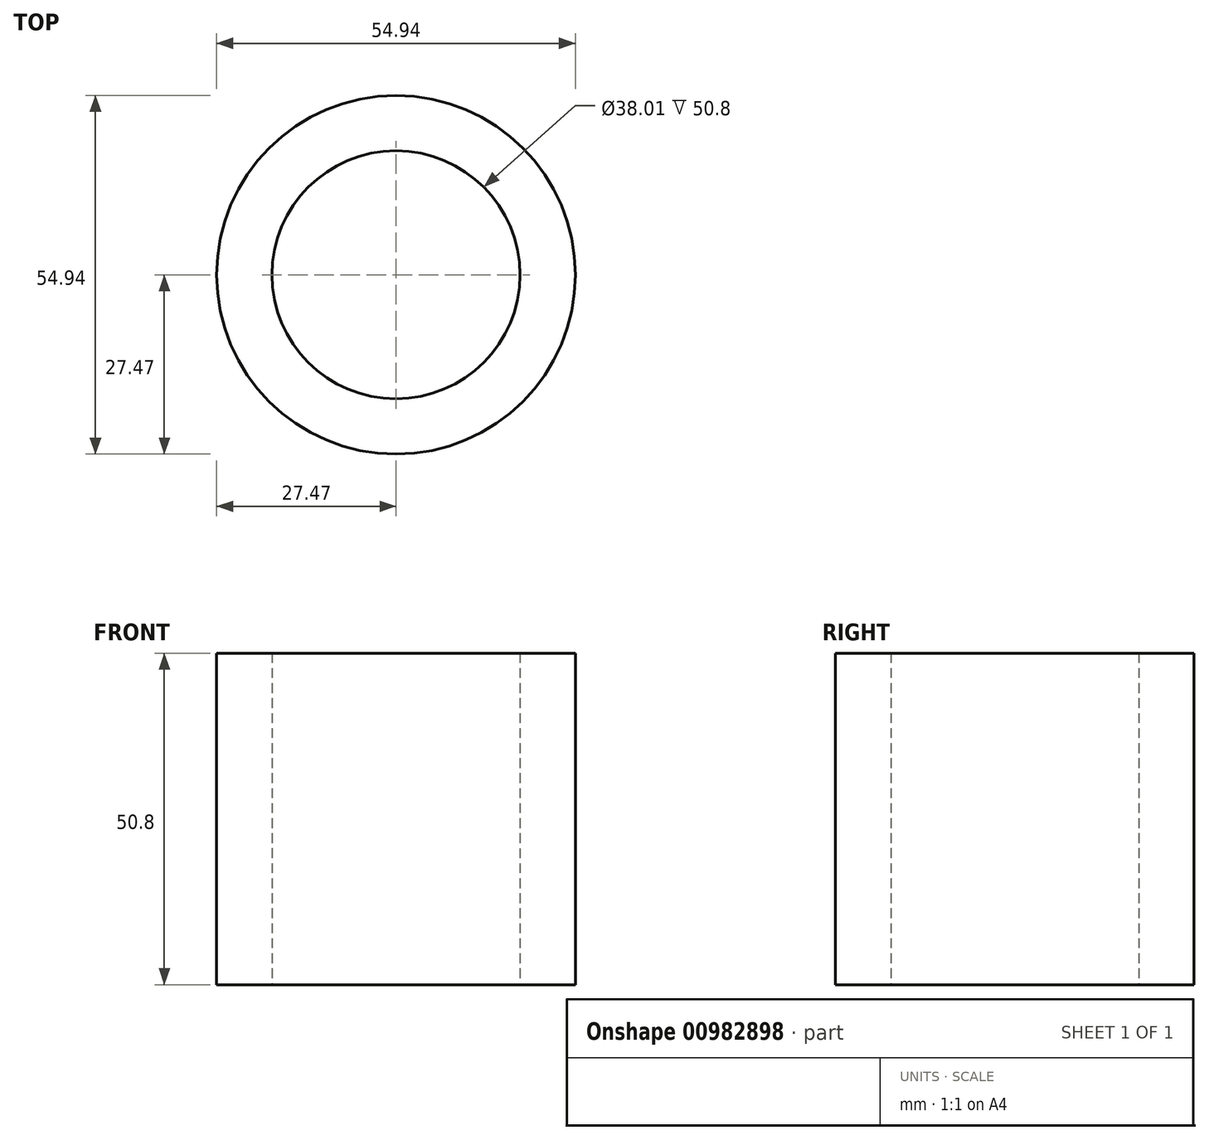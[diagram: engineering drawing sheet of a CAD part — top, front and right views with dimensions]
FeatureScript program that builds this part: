
annotation { "Feature Type Name" : "Feature", "Feature Type Description" : "" }
export const myFeature = defineFeature(function(context is Context, id is Id, definition is map)
    precondition{}
    {
        {
            var Q0;
            Q0=qCreatedBy(makeId("Top.planeOp"),FACE);
            var sketch = newSketch(context, id + "F0", { "sketchPlane" : qUnion([Q0])});
            skCircle(sketch, "E0", {"center": v(0, 0) * mm, "radius": 27.47 * mm});
            skCircle(sketch, "E1", {"center": v(0, 0) * mm, "radius": 19 * mm});
            skSolve(sketch);
        }
        {
            var Q0;
            Q0=makeQuery(id+"F0.imprint","IMPRINT",FACE,{"disambiguationData":[TD([[makeQuery(id+"F0.imprint","IMPRINT",EDGE,{"derivedFrom":sQuery(id+"F0.wireOp",EDGE,"E0")}),1.0]])]});
            extrude(context, id + "F1", {"entities" : qUnion([Q0]), "depth" : 50.8 * mm, "offsetDistance" : 25.4 * mm});
        }
    });
